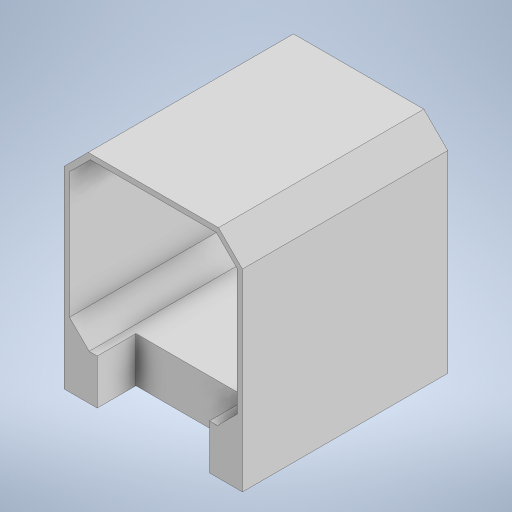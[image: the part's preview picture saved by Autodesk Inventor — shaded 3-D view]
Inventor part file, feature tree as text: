
AUTODESK INVENTOR PART (.ipt)
format: ipt  version: 2024.2 (Build 282272000, 272)  size: 624,128 bytes
history: native  units: mm
features: reference x37, extrude x4, sketch x4, other x3, projected_geometry x2
ambient origin geometry x8: Origin, YZ Plane, XZ Plane, XY Plane, X Axis, Y Axis, Z Axis, Center Point
bodies: Solid1 (feature_tree)
feature tree (50):
  extrude  "Extrusion1"  Depth=43.0mm TaperAngle=0.0deg
  extrude  "Extrusion2"  Depth=9.0mm TaperAngle=0.0deg
  extrude  "Extrusion3"  [1 undecoded]
  extrude  "Extrusion5"  [1 undecoded]
  sketch  "Sketch1"  dims[d0=5.0mm d1=0.0mm d2=43.0mm d3=0.0mm]
  reference  "Reference1"
  reference  "Reference2"
  reference  "Reference3"
  reference  "Reference4"
  reference  "Reference5"
  reference  "Reference6"
  reference  "Reference7"
  reference  "Reference8"
  reference  "Reference9"
  reference  "Reference10"
  reference  "Reference11"
  reference  "Reference12"
  reference  "Reference13"
  reference  "Reference14"
  reference  "Reference15"
  reference  "Reference16"
  reference  "Reference17"
  reference  "Reference18"
  reference  "Reference19"
  reference  "Reference20"
  reference  "Reference21"
  sketch  "Sketch2"  dims[d4=10.0mm d5=0.0mm d10=9.0mm d11=0.0mm]
  reference  "Reference22"
  reference  "Reference23"
  reference  "Reference24"
  reference  "Reference25"
  reference  "Reference26"
  projected_geometry  "Projected Loop1"
  reference  "Reference27"
  reference  "Reference28"
  reference  "Reference29"
  reference  "Reference30"
  reference  "Reference31"
  reference  "Reference32"
  sketch  "Sketch3"
  reference  "Reference33"
  reference  "Reference34"
  reference  "Reference35"
  reference  "Reference36"
  projected_geometry  "Projected Loop2"
  reference  "Reference37"
  sketch  "Sketch4"
  other  "<userpath>\Desktop\meca_robotbebou\embasev2\embasev2.iam"
  other  "embasev2.iam"
  other  "support_moteurv3:1"
note: 2 required parameter values undecoded (feature->parameter linkage not recoverable at this tier; creation-order binding heuristic only, values carry confidence <= 0.55)
